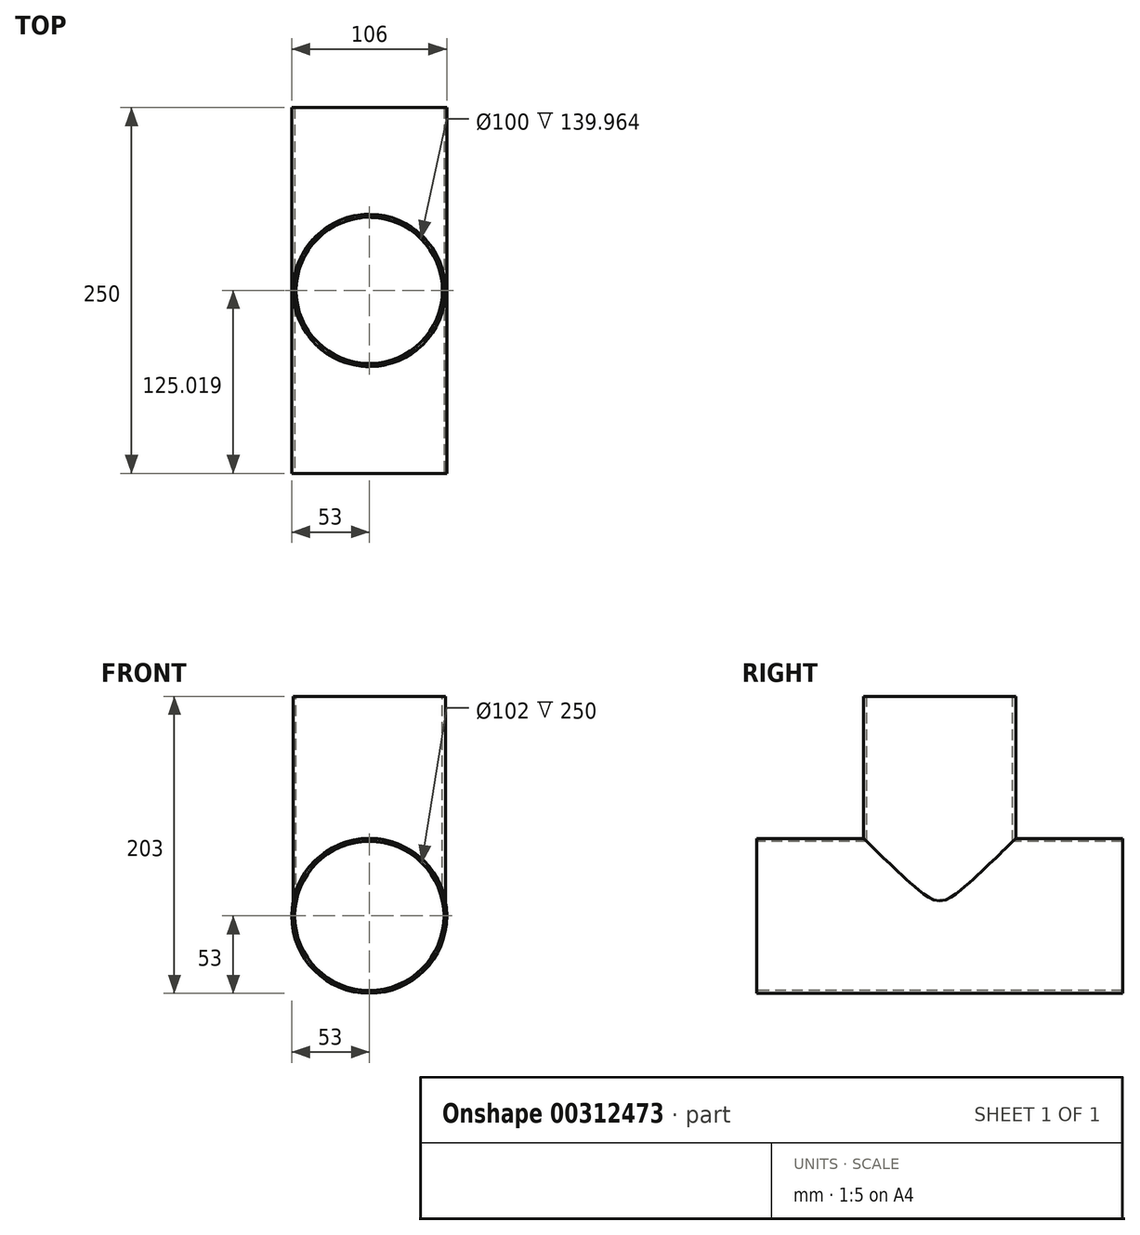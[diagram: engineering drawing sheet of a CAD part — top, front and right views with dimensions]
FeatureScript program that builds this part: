
annotation { "Feature Type Name" : "Feature", "Feature Type Description" : "" }
export const myFeature = defineFeature(function(context is Context, id is Id, definition is map)
    precondition{}
    {
        {
            var Q0;
            Q0=qCreatedBy(makeId("Front.planeOp"),FACE);
            var sketch = newSketch(context, id + "F0", { "sketchPlane" : qUnion([Q0])});
            skCircle(sketch, "E0", {"center": v(0, 0) * mm, "radius": 51 * mm});
            skCircle(sketch, "E1.0", {"center": v(0, 0) * mm, "radius": 53 * mm});
            skSolve(sketch);
        }
        {
            var Q0;
            Q0 = qSketchRegion(id + "F0", true);
            extrude(context, id + "F1", {"entities" : qUnion([Q0]), "oppositeDirection" : true, "depth" : 250 * mm});
        }
        {
            var Q0;
            Q0=qCreatedBy(makeId("Top.planeOp"),FACE);
            cPlane(context, id + "F2", {"entities" : qUnion([Q0]), "cplaneType" : CPlaneType.OFFSET, "offset" : 150 * mm, "width" : 150 * mm, "height" : 150 * mm});
        }
        {
            var Q0;
            Q0=qCreatedBy(id+"F2.planeOp",FACE);
            var sketch = newSketch(context, id + "F3", { "sketchPlane" : qUnion([Q0])});
            skLineSegment(sketch, "E2", {"start": v(0, 0) * mm, "end": v(0, 250.04) * mm, "construction": true});
            skCircle(sketch, "E3", {"center": v(0, 125.02) * mm, "radius": 50 * mm});
            skCircle(sketch, "E4.0", {"center": v(0, 125.02) * mm, "radius": 52 * mm});
            skSolve(sketch);
        }
        {
            var Q0;
            Q0 = qSketchRegion(id + "F3", true);
            var Q1;
            Q1=makeQuery(id+"F1.opExtrude","SWEPT_FACE",FACE,{"disambiguationData":[OSD([sQuery(id+"F0.wireOp",EDGE,"E1.0")])]});
            extrude(context, id + "F4", {"entities" : qUnion([Q0]), "operationType" : NewBodyOperationType.ADD, "endBound" : BoundingType.UP_TO_SURFACE, "oppositeDirection" : true, "endBoundEntityFace" : qUnion([Q1]), "depth" : 25 * mm});
        }
        {
            var Q0;
            Q0=qCreatedBy(id+"F2.planeOp",FACE);
            var sketch = newSketch(context, id + "F5", { "sketchPlane" : qUnion([Q0])});
            skCircle(sketch, "E5.0", {"center": v(0, 125.02) * mm, "radius": 50 * mm});
            skSolve(sketch);
        }
        {
            var Q0;
            Q0 = qSketchRegion(id + "F5", true);
            var Q1;
            Q1=makeQuery(id+"F1.opExtrude","SWEPT_FACE",FACE,{"disambiguationData":[OSD([sQuery(id+"F0.wireOp",EDGE,"E0")])]});
            extrude(context, id + "F6", {"entities" : qUnion([Q0]), "operationType" : NewBodyOperationType.REMOVE, "endBound" : BoundingType.UP_TO_SURFACE, "oppositeDirection" : true, "endBoundEntityFace" : qUnion([Q1]), "depth" : 25 * mm});
        }
    });
